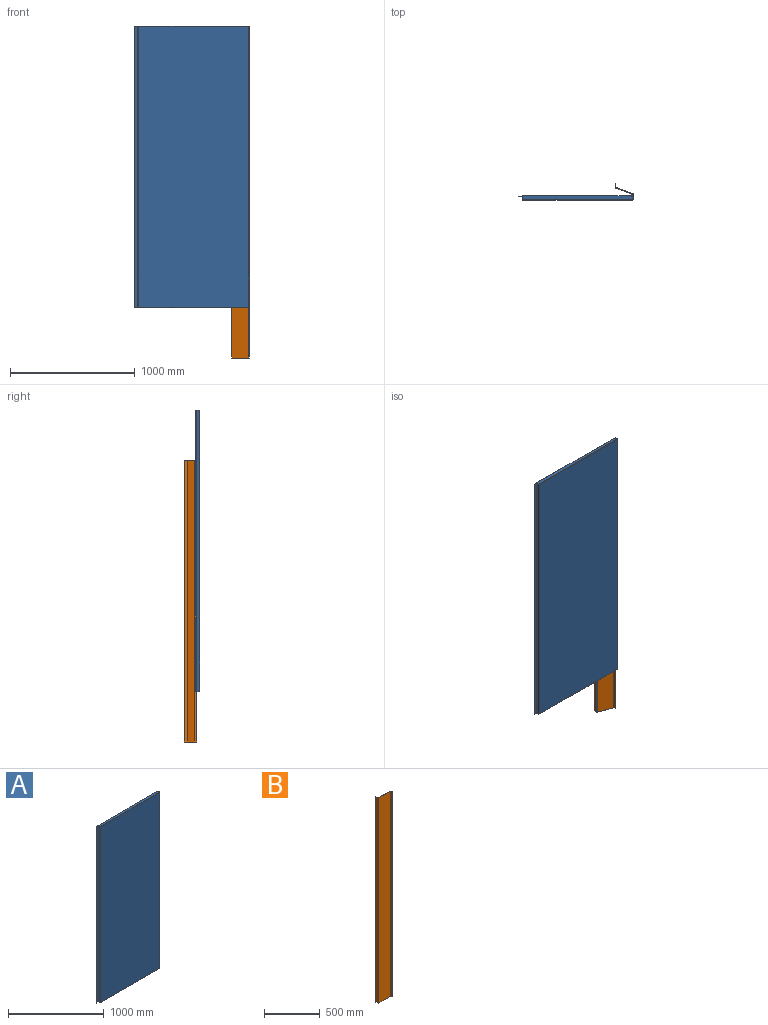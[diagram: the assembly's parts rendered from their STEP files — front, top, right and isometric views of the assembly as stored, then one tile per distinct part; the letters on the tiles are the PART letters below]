
ASSEMBLY  parts=2 mates=2
PART A: 80 faces, bbox 916x32.8x2255 mm
  f0: plane 886x26mm, normal (0,0,1), area 22994.6mm2, adj f11,f12,f14,f15,f16,f17,f18,f22
  f1: plane 2247x880mm, normal (0,1,0), area 1977354.8mm2, adj f3,f4,f5,f6,f7,f8,f9,f10
  f2: plane 2247x880mm, normal (0,-1,0), area 1977354.8mm2, adj f3,f4,f5,f6,f7,f8,f9,f10
  f3: plane 2x1.14mm, normal (0,0,1), area 2.3mm2, adj f1,f2,f4,f51
  f4: plane 2x1.14mm, normal (1,0,0), area 2.3mm2, adj f1,f2,f3,f32
  f5: plane 2x1.14mm, normal (1,0,0), area 2.3mm2, adj f1,f2,f6,f20
  f6: plane 2x1.14mm, normal (0,0,-1), area 2.3mm2, adj f1,f2,f5,f50
  f7: plane 2x1.14mm, normal (0,0,-1), area 2.3mm2, adj f1,f2,f8,f71
  f8: plane 2x1.14mm, normal (-1,0,0), area 2.3mm2, adj f1,f2,f7,f19
  f9: plane 2x1.14mm, normal (-1,0,0), area 2.3mm2, adj f1,f2,f10,f33
  f10: plane 2x1.14mm, normal (0,0,1), area 2.3mm2, adj f1,f2,f9,f72
  f11: plane 6x2mm, normal (-1,0,0), area 12mm2, adj f0,f13,f14,f69
  f12: plane 24.86x2mm, normal (1,0,0), area 49.7mm2, adj f0,f13,f14,f18,f37
  f13: plane 886x26mm, normal (0,0,-1), area 23026.6mm2, adj f11,f12,f14,f15,f16,f17,f18,f21
  f14: plane 886x2mm, normal (0,1,0), area 1772mm2, adj f0,f11,f12,f13
  f15: plane 2x1.14mm, normal (-1,0,0), area 2.3mm2, adj f0,f13,f16,f19
  f16: plane 3.14x2mm, normal (0,-1,0), area 6.3mm2, adj f0,f13,f15,f66
  f17: plane 2x1.14mm, normal (1,0,0), area 2.3mm2, adj f0,f13,f18,f20
  f18: plane 5.14x2mm, normal (0,-1,0), area 10.3mm2, adj f0,f12,f13,f17,f45
  f19: plane 4x4mm, normal (-1,0,0), area 9.4mm2, adj f8,f15,f21,f22
  f20: plane 4x4mm, normal (1,0,0), area 9.4mm2, adj f5,f17,f21,f22
  f21: cylinder r=4mm len=877.72mm, axis (-1,0,0), area 5514.9mm2, adj f2,f13,f19,f20
  f22: cylinder r=2mm len=877.72mm, axis (-1,0,0), area 2757.4mm2, adj f0,f1,f19,f20
  f23: plane 24.86x2mm, normal (1,0,0), area 49.7mm2, adj f25,f26,f27,f29,f37
  f24: plane 6x2mm, normal (-1,0,0), area 12mm2, adj f25,f26,f27,f69
  f25: plane 886x26mm, normal (0,0,1), area 23026.6mm2, adj f23,f24,f26,f28,f29,f30,f31,f34
  f26: plane 886x2mm, normal (0,1,0), area 1772mm2, adj f23,f24,f25,f27
  f27: plane 886x26mm, normal (0,0,-1), area 22994.6mm2, adj f23,f24,f26,f28,f29,f30,f31,f35
  f28: plane 2x1.14mm, normal (1,0,0), area 2.3mm2, adj f25,f27,f29,f32
  f29: plane 5.14x2mm, normal (0,-1,0), area 10.3mm2, adj f23,f25,f27,f28,f39
  f30: plane 2x1.14mm, normal (-1,0,0), area 2.3mm2, adj f25,f27,f31,f33
  f31: plane 3.14x2mm, normal (0,-1,0), area 6.3mm2, adj f25,f27,f30,f64
  f32: plane 4x4mm, normal (1,0,0), area 9.4mm2, adj f4,f28,f34,f35
  f33: plane 4x4mm, normal (-1,0,0), area 9.4mm2, adj f9,f30,f34,f35
  f34: cylinder r=4mm len=877.72mm, axis (1,0,0), area 5514.9mm2, adj f2,f25,f32,f33
  f35: cylinder r=2mm len=877.72mm, axis (1,0,0), area 2757.4mm2, adj f1,f27,f32,f33
  f36: plane 2251x19.2mm, normal (-1,0,0), area 43201.9mm2, adj f0,f27,f38,f39,f40,f41,f42,f43
  f37: plane 2251x19.2mm, normal (1,0,0), area 43201.9mm2, adj f12,f23,f38,f39,f40,f41,f42,f43
  f38: plane 2x1.14mm, normal (0,0,1), area 2.3mm2, adj f36,f37,f39,f51
  f39: plane 3.14x2mm, normal (0,-1,0), area 6.3mm2, adj f29,f36,f37,f38
  f40: plane 2x2mm, normal (0,1,0), area 4mm2, adj f27,f36,f37,f41
  f41: plane 2.06x2mm, normal (0,0,1), area 4.1mm2, adj f36,f37,f40,f46
  f42: plane 2x2mm, normal (0,1,0), area 4mm2, adj f0,f36,f37,f43
  f43: plane 2.06x2mm, normal (0,0,-1), area 4.1mm2, adj f36,f37,f42,f47
  f44: plane 2x1.14mm, normal (0,0,-1), area 2.3mm2, adj f36,f37,f45,f50
  f45: plane 3.14x2mm, normal (0,-1,0), area 6.3mm2, adj f18,f36,f37,f44
  f46: plane 3.76x3.32mm, normal (0,0,1), area 7.3mm2, adj f41,f48,f49,f56
  f47: plane 3.76x3.32mm, normal (0,0,-1), area 7.3mm2, adj f43,f48,f49,f55
  f48: cylinder r=4mm len=2247mm, axis (0,0,1), area 10980.9mm2, adj f37,f46,f47,f58
  f49: cylinder r=2mm len=2247mm, axis (0,0,1), area 5490.5mm2, adj f36,f46,f47,f57
  f50: plane 4x4mm, normal (0,0,-1), area 9.4mm2, adj f6,f44,f52,f53
  f51: plane 4x4mm, normal (0,0,1), area 9.4mm2, adj f3,f38,f52,f53
  f52: cylinder r=4mm len=2244.72mm, axis (0,0,-1), area 14104mm2, adj f2,f37,f50,f51
  f53: cylinder r=2mm len=2244.72mm, axis (0,0,-1), area 7052mm2, adj f1,f36,f50,f51
  f54: plane 2247x1.88mm, normal (-0.94,0.34,0), area 4494mm2, adj f55,f56,f57,f58
  f55: plane 16.85x7.76mm, normal (0,0,-1), area 34.4mm2, adj f47,f54,f57,f58
  f56: plane 16.85x7.76mm, normal (0,0,1), area 34.4mm2, adj f46,f54,f57,f58
  f57: plane 2247x16.16mm, normal (-0.34,-0.94,0), area 38646.5mm2, adj f49,f54,f55,f56
  f58: plane 2247x16.16mm, normal (0.34,0.94,0), area 38646.5mm2, adj f48,f54,f55,f56
  f59: plane 18.86x2mm, normal (0,0,1), area 37.7mm2, adj f25,f61,f64,f67
  f60: plane 18.86x2mm, normal (0,0,-1), area 37.7mm2, adj f13,f61,f66,f68
  f61: plane 2255x20mm, normal (-1,0,0), area 45088.3mm2, adj f59,f60,f63,f64,f65,f66,f70,f73
  f62: plane 2251x20mm, normal (1,0,0), area 45012.9mm2, adj f0,f27,f63,f64,f65,f66,f69,f74
  f63: plane 2x1.14mm, normal (0,0,1), area 2.3mm2, adj f61,f62,f64,f72
  f64: plane 5.14x2mm, normal (0,-1,0), area 10.3mm2, adj f31,f59,f61,f62,f63
  f65: plane 2x1.14mm, normal (0,0,-1), area 2.3mm2, adj f61,f62,f66,f71
  f66: plane 5.14x2mm, normal (0,-1,0), area 10.3mm2, adj f16,f60,f61,f62,f65
  f67: plane 4x4mm, normal (0,0,1), area 9.4mm2, adj f59,f69,f70,f76
  f68: plane 4x4mm, normal (0,0,-1), area 9.4mm2, adj f60,f69,f70,f77
  f69: cylinder r=4mm len=2255mm, axis (0,0,1), area 14168.6mm2, adj f11,f24,f62,f67,f68,f78
  f70: cylinder r=2mm len=2255mm, axis (0,0,1), area 7084.3mm2, adj f61,f67,f68,f79
  f71: plane 4x4mm, normal (0,0,-1), area 9.4mm2, adj f7,f65,f73,f74
  f72: plane 4x4mm, normal (0,0,1), area 9.4mm2, adj f10,f63,f73,f74
  f73: cylinder r=4mm len=2244.72mm, axis (0,0,-1), area 14104mm2, adj f2,f61,f71,f72
  f74: cylinder r=2mm len=2244.72mm, axis (0,0,-1), area 7052mm2, adj f1,f62,f71,f72
  f75: plane 2255x2mm, normal (-1,0,0), area 4510mm2, adj f76,f77,f78,f79
  f76: plane 26x2mm, normal (0,0,1), area 52mm2, adj f67,f75,f78,f79
  f77: plane 26x2mm, normal (0,0,-1), area 52mm2, adj f68,f75,f78,f79
  f78: plane 2255x26mm, normal (0,1,0), area 58630mm2, adj f69,f75,f76,f77
  f79: plane 2255x26mm, normal (0,-1,0), area 58630mm2, adj f70,f75,f76,f77
PART B: 22 faces, bbox 167.1x46.4x2251 mm
  f0: plane 144.4x2mm, normal (0,0,-1), area 288.8mm2, adj f2,f3,f10,f18
  f1: plane 144.4x2mm, normal (0,0,1), area 288.8mm2, adj f2,f3,f9,f19
  f2: plane 2251x144.4mm, normal (0,1,0), area 325040.7mm2, adj f0,f1,f11,f21
  f3: plane 2251x144.4mm, normal (0,-1,0), area 325040.7mm2, adj f0,f1,f12,f20
  f4: plane 2251x1.88mm, normal (0.34,-0.94,0), area 4502mm2, adj f5,f6,f7,f8
  f5: plane 16.85x7.76mm, normal (0,0,-1), area 34.4mm2, adj f4,f7,f8,f10
  f6: plane 16.85x7.76mm, normal (0,0,1), area 34.4mm2, adj f4,f7,f8,f9
  f7: plane 2251x16.16mm, normal (0.94,0.34,0), area 38715.3mm2, adj f4,f5,f6,f11
  f8: plane 2251x16.16mm, normal (-0.94,-0.34,0), area 38715.3mm2, adj f4,f5,f6,f12
  f9: plane 3.76x3.32mm, normal (0,0,1), area 7.3mm2, adj f1,f6,f11,f12
  f10: plane 3.76x3.32mm, normal (0,0,-1), area 7.3mm2, adj f0,f5,f11,f12
  f11: cylinder r=4mm len=2251mm, axis (0,0,1), area 11000.5mm2, adj f2,f7,f9,f10
  f12: cylinder r=2mm len=2251mm, axis (0,0,1), area 5500.2mm2, adj f3,f8,f9,f10
  f13: plane 2251x1.88mm, normal (-0.34,0.94,0), area 4502mm2, adj f14,f15,f16,f17
  f14: plane 26.24x11.18mm, normal (0,0,1), area 54.4mm2, adj f13,f16,f17,f19
  f15: plane 26.24x11.18mm, normal (0,0,-1), area 54.4mm2, adj f13,f16,f17,f18
  f16: plane 2251x25.56mm, normal (0.94,0.34,0), area 61225.3mm2, adj f13,f14,f15,f21
  f17: plane 2251x25.56mm, normal (-0.94,-0.34,0), area 61225.3mm2, adj f13,f14,f15,f20
  f18: plane 3.76x3.32mm, normal (0,0,-1), area 7.3mm2, adj f0,f15,f20,f21
  f19: plane 3.76x3.32mm, normal (0,0,1), area 7.3mm2, adj f1,f14,f20,f21
  f20: cylinder r=4mm len=2251mm, axis (0,0,-1), area 11000.5mm2, adj f3,f17,f18,f19
  f21: cylinder r=2mm len=2251mm, axis (0,0,-1), area 5500.2mm2, adj f2,f16,f18,f19
PLACE A t=(433.69,2,-763.03)mm
PLACE B rot(axis=(0,0,-1),20deg) t=(822.75,70.29,-1385.84)mm
MATE planar B.f8 <-> A.f23  axis (-1,0,0) through (884,35.86,720.68)mm
MATE planar B.f8 <-> A.f23  axis (-1,0,0) through (884,35.86,720.68)mm
